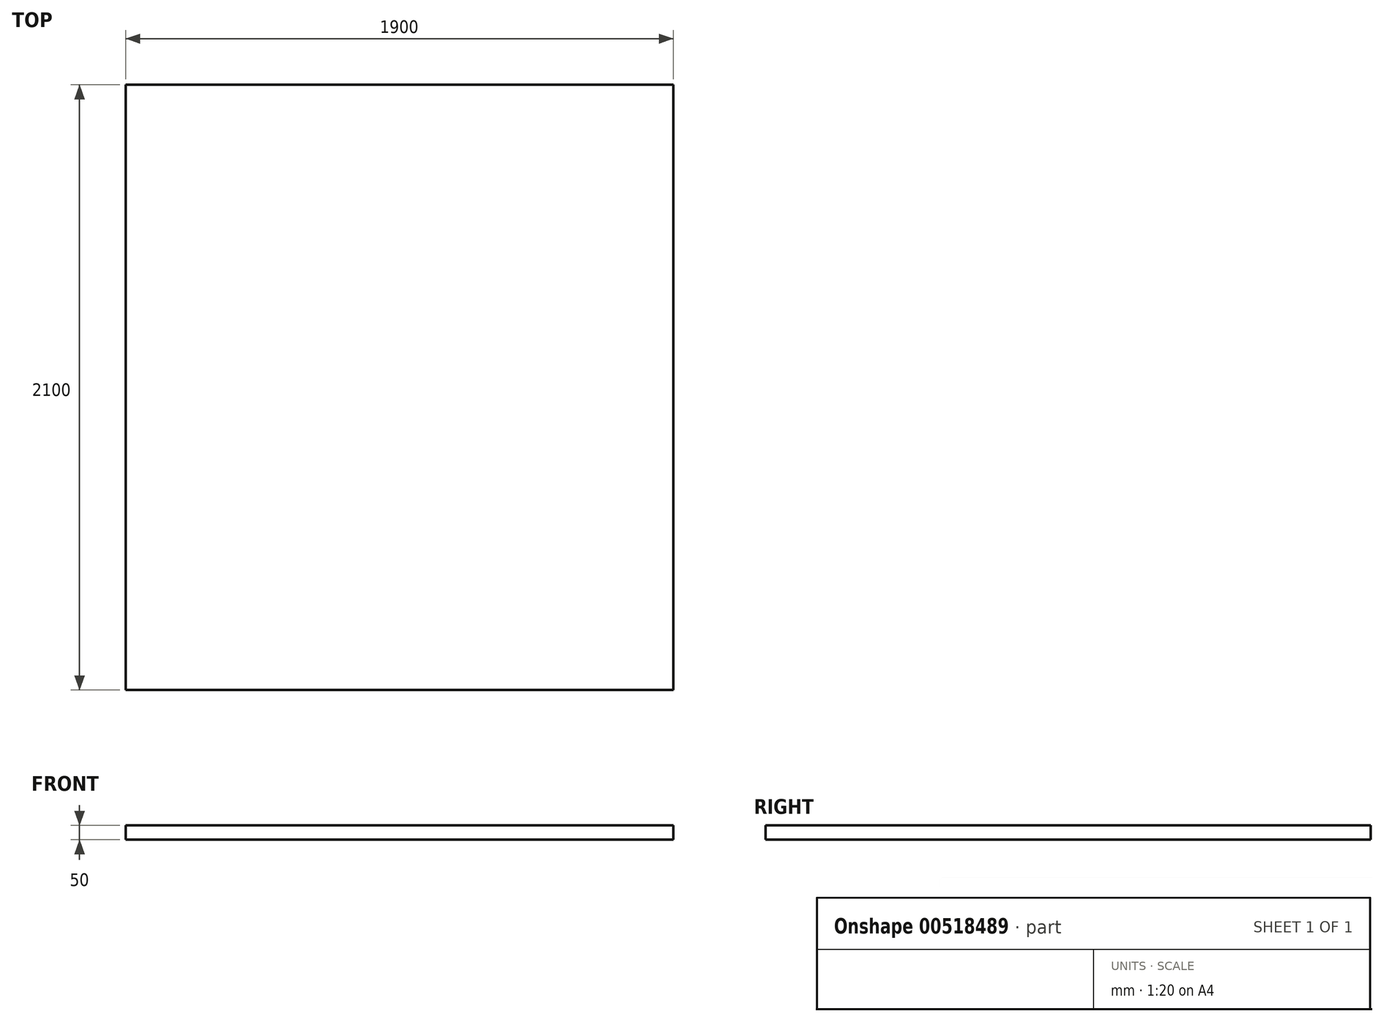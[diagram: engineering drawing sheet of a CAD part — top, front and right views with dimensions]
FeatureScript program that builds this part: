
annotation { "Feature Type Name" : "Feature", "Feature Type Description" : "" }
export const myFeature = defineFeature(function(context is Context, id is Id, definition is map)
    precondition{}
    {
        {
            var Q0;
            Q0=qCreatedBy(makeId("Top.planeOp"),FACE);
            var sketch = newSketch(context, id + "F0", { "sketchPlane" : qUnion([Q0])});
            skLineSegment(sketch, "E0.bottom", {"start": v(950, -1050) * mm, "end": v(-950, -1050) * mm});
            skLineSegment(sketch, "E0.top", {"start": v(950, 1050) * mm, "end": v(-950, 1050) * mm});
            skLineSegment(sketch, "E0.left", {"start": v(950, -1050) * mm, "end": v(950, 1050) * mm});
            skLineSegment(sketch, "E0.right", {"start": v(-950, -1050) * mm, "end": v(-950, 1050) * mm});
            skPoint(sketch, "E0.middle", {"position": v(0, 0) * mm});
            skLineSegment(sketch, "E1", {"start": v(0, 1050) * mm, "end": v(0, -1050) * mm, "construction": true});
            skLineSegment(sketch, "E2", {"start": v(-950, 0) * mm, "end": v(950, 0) * mm, "construction": true});
            skLineSegment(sketch, "E3.bottom", {"start": v(-925, -875) * mm, "end": v(-775, -875) * mm});
            skLineSegment(sketch, "E3.top", {"start": v(-925, -1025) * mm, "end": v(-775, -1025) * mm});
            skLineSegment(sketch, "E3.left", {"start": v(-925, -875) * mm, "end": v(-925, -1025) * mm});
            skLineSegment(sketch, "E3.right", {"start": v(-775, -875) * mm, "end": v(-775, -1025) * mm});
            skLineSegment(sketch, "E4.MirrorCS", {"start": v(-925, 1025) * mm, "end": v(-775, 1025) * mm});
            skLineSegment(sketch, "E5.MirrorCS", {"start": v(-925, 875) * mm, "end": v(-925, 1025) * mm});
            skLineSegment(sketch, "E6.MirrorCS", {"start": v(-925, 875) * mm, "end": v(-775, 875) * mm});
            skLineSegment(sketch, "E7.MirrorCS", {"start": v(-775, 875) * mm, "end": v(-775, 1025) * mm});
            skLineSegment(sketch, "E8.MirrorCS", {"start": v(925, 875) * mm, "end": v(775, 875) * mm});
            skLineSegment(sketch, "E9.MirrorCS", {"start": v(925, 875) * mm, "end": v(925, 1025) * mm});
            skLineSegment(sketch, "E10.MirrorCS", {"start": v(925, 1025) * mm, "end": v(775, 1025) * mm});
            skLineSegment(sketch, "E11.MirrorCS", {"start": v(775, 875) * mm, "end": v(775, 1025) * mm});
            skLineSegment(sketch, "E12.MirrorCS", {"start": v(925, -1025) * mm, "end": v(775, -1025) * mm});
            skLineSegment(sketch, "E13.MirrorCS", {"start": v(925, -875) * mm, "end": v(925, -1025) * mm});
            skLineSegment(sketch, "E14.MirrorCS", {"start": v(925, -875) * mm, "end": v(775, -875) * mm});
            skLineSegment(sketch, "E15.MirrorCS", {"start": v(775, -875) * mm, "end": v(775, -1025) * mm});
            skLineSegment(sketch, "E16", {"start": v(-900, -475) * mm, "end": v(-800, -475) * mm, "construction": true});
            skLineSegment(sketch, "E17.MirrorCS", {"start": v(-925, 75) * mm, "end": v(-775, 75) * mm});
            skLineSegment(sketch, "E18.MirrorCS", {"start": v(-925, -75) * mm, "end": v(-775, -75) * mm});
            skLineSegment(sketch, "E19.MirrorCS", {"start": v(-925, -75) * mm, "end": v(-925, 75) * mm});
            skLineSegment(sketch, "E20.MirrorCS", {"start": v(-775, -75) * mm, "end": v(-775, 75) * mm});
            skLineSegment(sketch, "E21.MirrorCS", {"start": v(925, 75) * mm, "end": v(775, 75) * mm});
            skLineSegment(sketch, "E22.MirrorCS", {"start": v(925, -75) * mm, "end": v(925, 75) * mm});
            skLineSegment(sketch, "E23.MirrorCS", {"start": v(775, -75) * mm, "end": v(775, 75) * mm});
            skLineSegment(sketch, "E24.MirrorCS", {"start": v(925, -75) * mm, "end": v(775, -75) * mm});
            skLineSegment(sketch, "E25", {"start": v(-587.5, -900) * mm, "end": v(-587.5, -1000) * mm, "construction": true});
            skLineSegment(sketch, "E26.MirrorCS", {"start": v(-250, -1025) * mm, "end": v(-400, -1025) * mm});
            skLineSegment(sketch, "E27.MirrorCS", {"start": v(-400, -875) * mm, "end": v(-400, -1025) * mm});
            skLineSegment(sketch, "E28.MirrorCS", {"start": v(-250, -875) * mm, "end": v(-400, -875) * mm});
            skLineSegment(sketch, "E29.MirrorCS", {"start": v(-250, -875) * mm, "end": v(-250, -1025) * mm});
            skLineSegment(sketch, "E30", {"start": v(-775, -950) * mm, "end": v(-400, -950) * mm, "construction": true});
            skLineSegment(sketch, "E31", {"start": v(-775, -1000) * mm, "end": v(-400, -1000) * mm});
            skLineSegment(sketch, "E32.MirrorCS", {"start": v(-775, -900) * mm, "end": v(-400, -900) * mm});
            skLineSegment(sketch, "E33", {"start": v(-850, -75) * mm, "end": v(-850, -875) * mm, "construction": true});
            skLineSegment(sketch, "E34", {"start": v(-900, -75) * mm, "end": v(-900, -875) * mm});
            skLineSegment(sketch, "E35.MirrorCS", {"start": v(-800, -75) * mm, "end": v(-800, -875) * mm});
            skLineSegment(sketch, "E36.MirrorCS", {"start": v(-800, 75) * mm, "end": v(-800, 875) * mm});
            skLineSegment(sketch, "E37.MirrorCS", {"start": v(-900, 75) * mm, "end": v(-900, 875) * mm});
            skLineSegment(sketch, "E38.MirrorCS", {"start": v(775, -1000) * mm, "end": v(400, -1000) * mm});
            skLineSegment(sketch, "E39.MirrorCS", {"start": v(775, -900) * mm, "end": v(400, -900) * mm});
            skLineSegment(sketch, "E40.MirrorCS", {"start": v(900, -75) * mm, "end": v(900, -875) * mm});
            skLineSegment(sketch, "E41.MirrorCS", {"start": v(800, -75) * mm, "end": v(800, -875) * mm});
            skLineSegment(sketch, "E42.MirrorCS", {"start": v(800, 75) * mm, "end": v(800, 875) * mm});
            skLineSegment(sketch, "E43.MirrorCS", {"start": v(900, 75) * mm, "end": v(900, 875) * mm});
            skLineSegment(sketch, "E44.MirrorCS", {"start": v(250, -875) * mm, "end": v(400, -875) * mm});
            skLineSegment(sketch, "E45.MirrorCS", {"start": v(250, -875) * mm, "end": v(250, -1025) * mm});
            skLineSegment(sketch, "E46.MirrorCS", {"start": v(250, -1025) * mm, "end": v(400, -1025) * mm});
            skLineSegment(sketch, "E47.MirrorCS", {"start": v(400, -875) * mm, "end": v(400, -1025) * mm});
            skLineSegment(sketch, "E48.bottom", {"start": v(-775, 1025) * mm, "end": v(775, 1025) * mm});
            skLineSegment(sketch, "E48.top", {"start": v(-775, 825) * mm, "end": v(775, 825) * mm});
            skLineSegment(sketch, "E48.left", {"start": v(-775, 1025) * mm, "end": v(-775, 825) * mm});
            skLineSegment(sketch, "E48.right", {"start": v(775, 1025) * mm, "end": v(775, 825) * mm});
            skLineSegment(sketch, "E49.bottom", {"start": v(10, 1000) * mm, "end": v(760, 1000) * mm});
            skLineSegment(sketch, "E49.top", {"start": v(10, 880) * mm, "end": v(760, 880) * mm});
            skLineSegment(sketch, "E49.left", {"start": v(10, 1000) * mm, "end": v(10, 880) * mm});
            skLineSegment(sketch, "E49.right", {"start": v(760, 1000) * mm, "end": v(760, 880) * mm});
            skLineSegment(sketch, "E50", {"start": v(10, 900) * mm, "end": v(760, 900) * mm});
            skSolve(sketch);
        }
        {
            var Q0;
            Q0=qCreatedBy(makeId("Top.planeOp"),FACE);
            var sketch = newSketch(context, id + "F1", { "sketchPlane" : qUnion([Q0])});
            skLineSegment(sketch, "E51.0", {"start": v(-950, -1050) * mm, "end": v(-950, 1050) * mm});
            skLineSegment(sketch, "E51.1", {"start": v(950, 1050) * mm, "end": v(-950, 1050) * mm});
            skLineSegment(sketch, "E51.2", {"start": v(950, -1050) * mm, "end": v(950, 1050) * mm});
            skLineSegment(sketch, "E51.3", {"start": v(950, -1050) * mm, "end": v(-950, -1050) * mm});
            skLineSegment(sketch, "E52.0", {"start": v(-750, -850) * mm, "end": v(-750, 800) * mm});
            skLineSegment(sketch, "E52.1", {"start": v(750, -850) * mm, "end": v(-750, -850) * mm, "construction": true});
            skLineSegment(sketch, "E52.2", {"start": v(750, -850) * mm, "end": v(750, 800) * mm});
            skLineSegment(sketch, "E53.0", {"start": v(950, 800) * mm, "end": v(-950, 800) * mm});
            skLineSegment(sketch, "E54", {"start": v(-950, -850) * mm, "end": v(950, -850) * mm});
            skSolve(sketch);
        }
        {
            var Q0;
            Q0=qCreatedBy(makeId("Top.planeOp"),FACE);
            var sketch = newSketch(context, id + "F2", { "sketchPlane" : qUnion([Q0])});
            skLineSegment(sketch, "E55.0", {"start": v(-925, -1025) * mm, "end": v(-925, 1025) * mm});
            skLineSegment(sketch, "E55.1", {"start": v(925, -1025) * mm, "end": v(-925, -1025) * mm});
            skLineSegment(sketch, "E55.2", {"start": v(925, -1025) * mm, "end": v(925, 1025) * mm});
            skLineSegment(sketch, "E55.3", {"start": v(925, 1025) * mm, "end": v(-925, 1025) * mm});
            skLineSegment(sketch, "E56.0", {"start": v(895, 995) * mm, "end": v(-895, 995) * mm});
            skLineSegment(sketch, "E56.1", {"start": v(895, -995) * mm, "end": v(895, 995) * mm});
            skLineSegment(sketch, "E56.2", {"start": v(895, -995) * mm, "end": v(-895, -995) * mm});
            skLineSegment(sketch, "E56.3", {"start": v(-895, -995) * mm, "end": v(-895, 995) * mm});
            skLineSegment(sketch, "E57", {"start": v(-925, 0) * mm, "end": v(925, 0) * mm, "construction": true});
            skLineSegment(sketch, "E58", {"start": v(0, 1025) * mm, "end": v(0, -1025) * mm, "construction": true});
            skSolve(sketch);
        }
        {
            var Q0;
            Q0=qCreatedBy(makeId("Front.planeOp"),FACE);
            var sketch = newSketch(context, id + "F3", { "sketchPlane" : qUnion([Q0])});
            skLineSegment(sketch, "E59.bottom", {"start": v(-950, 0) * mm, "end": v(950, 0) * mm});
            skLineSegment(sketch, "E59.top", {"start": v(-950, -50) * mm, "end": v(950, -50) * mm});
            skLineSegment(sketch, "E59.left", {"start": v(-950, 0) * mm, "end": v(-950, -50) * mm});
            skLineSegment(sketch, "E59.right", {"start": v(950, 0) * mm, "end": v(950, -50) * mm});
            skLineSegment(sketch, "E60", {"start": v(0, 0) * mm, "end": v(0, -250) * mm, "construction": true});
            skPoint(sketch, "E60.endSnap0", {"position": v(0, -50) * mm});
            skLineSegment(sketch, "E61", {"start": v(0, -250) * mm, "end": v(-925, -250) * mm});
            skLineSegment(sketch, "E62", {"start": v(-925, -250) * mm, "end": v(-925, -50) * mm});
            skLineSegment(sketch, "E63.MirrorCS", {"start": v(925, -250) * mm, "end": v(925, -50) * mm});
            skLineSegment(sketch, "E64.MirrorCS", {"start": v(0, -250) * mm, "end": v(925, -250) * mm});
            skLineSegment(sketch, "E65.bottom", {"start": v(-925, 0) * mm, "end": v(-775, 0) * mm});
            skLineSegment(sketch, "E65.top", {"start": v(-925, 300) * mm, "end": v(-775, 300) * mm});
            skLineSegment(sketch, "E65.left", {"start": v(-925, 0) * mm, "end": v(-925, 300) * mm});
            skLineSegment(sketch, "E65.right", {"start": v(-775, 0) * mm, "end": v(-775, 300) * mm});
            skLineSegment(sketch, "E66", {"start": v(-587.5, -50) * mm, "end": v(-587.5, -250) * mm, "construction": true});
            skLineSegment(sketch, "E67.MirrorCS", {"start": v(-400, 0) * mm, "end": v(-400, 300) * mm});
            skLineSegment(sketch, "E68.MirrorCS", {"start": v(-250, 300) * mm, "end": v(-400, 300) * mm});
            skLineSegment(sketch, "E69.MirrorCS", {"start": v(-250, 0) * mm, "end": v(-250, 300) * mm});
            skLineSegment(sketch, "E70.MirrorCS", {"start": v(-250, 0) * mm, "end": v(-400, 0) * mm});
            skLineSegment(sketch, "E71", {"start": v(-775, 200) * mm, "end": v(-400, 200) * mm});
            skLineSegment(sketch, "E72.MirrorCS", {"start": v(925, 0) * mm, "end": v(775, 0) * mm});
            skLineSegment(sketch, "E73.MirrorCS", {"start": v(925, 0) * mm, "end": v(925, 300) * mm});
            skLineSegment(sketch, "E74.MirrorCS", {"start": v(925, 300) * mm, "end": v(775, 300) * mm});
            skLineSegment(sketch, "E75.MirrorCS", {"start": v(775, 0) * mm, "end": v(775, 300) * mm});
            skLineSegment(sketch, "E76.MirrorCS", {"start": v(775, 200) * mm, "end": v(400, 200) * mm});
            skLineSegment(sketch, "E77.MirrorCS", {"start": v(250, 0) * mm, "end": v(400, 0) * mm});
            skLineSegment(sketch, "E78.MirrorCS", {"start": v(400, 0) * mm, "end": v(400, 300) * mm});
            skLineSegment(sketch, "E79.MirrorCS", {"start": v(250, 300) * mm, "end": v(400, 300) * mm});
            skLineSegment(sketch, "E80.MirrorCS", {"start": v(250, 0) * mm, "end": v(250, 300) * mm});
            skLineSegment(sketch, "E81", {"start": v(-775, 200) * mm, "end": v(775, 200) * mm});
            skLineSegment(sketch, "E82.bottom", {"start": v(10, 200) * mm, "end": v(760, 200) * mm});
            skLineSegment(sketch, "E82.top", {"start": v(10, 1600) * mm, "end": v(760, 1600) * mm});
            skLineSegment(sketch, "E82.left", {"start": v(10, 200) * mm, "end": v(10, 1600) * mm});
            skLineSegment(sketch, "E82.right", {"start": v(760, 200) * mm, "end": v(760, 1600) * mm});
            skSolve(sketch);
        }
        {
            var Q0;
            Q0=qCreatedBy(makeId("Top.planeOp"),FACE);
            var sketch = newSketch(context, id + "F4", { "sketchPlane" : qUnion([Q0])});
            skLineSegment(sketch, "E83.0", {"start": v(-950, -1050) * mm, "end": v(-950, 1050) * mm});
            skLineSegment(sketch, "E83.1", {"start": v(950, 1050) * mm, "end": v(-950, 1050) * mm});
            skLineSegment(sketch, "E83.2", {"start": v(950, -1050) * mm, "end": v(950, 1050) * mm});
            skLineSegment(sketch, "E83.3", {"start": v(950, -1050) * mm, "end": v(-950, -1050) * mm});
            skSolve(sketch);
        }
        {
            var Q0;
            Q0 = qSketchRegion(id + "F4", true);
            var Q1;
            Q1=sQuery(id+"F3.wireOp",VERTEX,"E62.end");
            extrude(context, id + "F5", {"entities" : qUnion([Q0]), "endBound" : BoundingType.UP_TO_VERTEX, "oppositeDirection" : true, "depth" : 102 * mm, "endBoundEntityVertex" : qUnion([Q1]), "offsetDistance" : 25 * mm});
        }
    });
